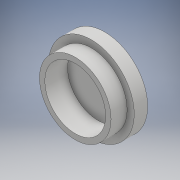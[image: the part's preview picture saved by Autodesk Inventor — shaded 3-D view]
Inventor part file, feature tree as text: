
AUTODESK INVENTOR PART (.ipt)
format: ipt  version: 2019 (Build 230136000, 136)  size: 260,608 bytes
history: native  units: mm
features: sketch x2, revolve x1, extrude x1
ambient origin geometry x8: Origin, YZ Plane, XZ Plane, XY Plane, X Axis, Y Axis, Z Axis, Center Point
bodies: Solid1 (feature_tree)
feature tree (4):
  revolve  "Revolution1"  [1 undecoded]
  extrude  "Extrusion2"  Depth=13.35mm
  sketch  "Sketch2"  dims[d4=16.0mm d5=5.0mm]
  sketch  "Sketch4"  dims[d6=6.0mm d8=13.35mm d10=90.0deg d14=2.0mm d15=0.0mm d16=11.35mm d17=2.0mm]
note: 1 required parameter value undecoded (feature->parameter linkage not recoverable at this tier; creation-order binding heuristic only, values carry confidence <= 0.55)
